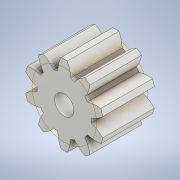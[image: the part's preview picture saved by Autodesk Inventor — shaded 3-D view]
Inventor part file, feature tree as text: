
AUTODESK INVENTOR PART (.ipt)
format: ipt  version: 2021 (Build 250183000, 183)  size: 227,840 bytes
history: native  units: mm (DEFAULTED — no unit token found)
features: plane x3, other x3, sketch x3, extrude x1, hole x1
ambient origin geometry x8: Origin, YZ Plane, XZ Plane, XY Plane, X Axis, Y Axis, Z Axis, Center Point
bodies: Solid1 (feature_tree)
feature tree (11):
  extrude  "Extrusion1"  Depth=8.0mm TaperAngle=0.0deg
  plane  "Work Plane2"
  plane  "Work Plane8"
  plane  "Work Plane9"
  other  "Spur Gear"
  hole  "Hole1"  [1 undecoded]
  sketch  "Sketch1"  dims[d0=12.303391mm d1=8.0mm d2=0.0mm]
  sketch  "Sketch2"  dims[d3=10.0mm d4=10.0mm d5=0.0mm]
  other  "Srf1"
  sketch  "Sketch3"  dims[d16=25.351695mm d17=0.0mm d34=3.141593mm d39=0.0mm d41=0.0mm d43=25.351695mm d46=25.351695mm d47=0.0mm d48=0.0mm d49=3.0mm d50=3.0mm d51=6.0mm d52=4.0mm d53=2.0mm d54=90.0deg d55=8.0mm d56=20.594885mm]
  other  "Pitch Diameter"
note: 1 required parameter value undecoded (feature->parameter linkage not recoverable at this tier; creation-order binding heuristic only, values carry confidence <= 0.55)
